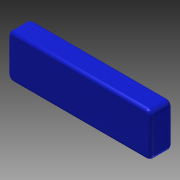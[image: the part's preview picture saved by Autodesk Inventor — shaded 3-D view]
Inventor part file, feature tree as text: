
AUTODESK INVENTOR PART (.ipt)
format: ipt  version: 2015 (Build 190159000, 159)  size: 117,760 bytes
history: native  units: mm
features: fillet x2, extrude x1, sketch x1
ambient origin geometry x8: Origin, YZ Plane, XZ Plane, XY Plane, X Axis, Y Axis, Z Axis, Center Point
bodies: Solid1 (feature_tree)
feature tree (4):
  extrude  "Extrusion1"  Depth=41.0mm
  fillet  "Fillet1"  Radius=20.0mm
  fillet  "Fillet2"  Radius=5.0mm
  sketch  "Sketch1"  dims[d0=135.0mm d1=41.0mm d2=20.0mm d3=0.0mm d4=5.0mm d5=3.0mm]
